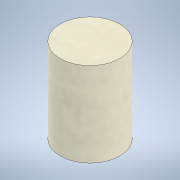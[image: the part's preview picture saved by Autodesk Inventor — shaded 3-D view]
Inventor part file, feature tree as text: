
AUTODESK INVENTOR PART (.ipt)
format: ipt  version: 2021 (Build 250183000, 183)  size: 100,864 bytes
history: native  units: mm
features: extrude x1, sketch x1
ambient origin geometry x8: Origin, YZ Plane, XZ Plane, XY Plane, X Axis, Y Axis, Z Axis, Center Point
bodies: Solid1 (feature_tree)
feature tree (2):
  extrude  "Extrusion1"  Depth=35.8mm TaperAngle=0.0deg
  sketch  "Sketch1"  dims[d0=25.25mm d1=35.8mm d2=0.0mm]
